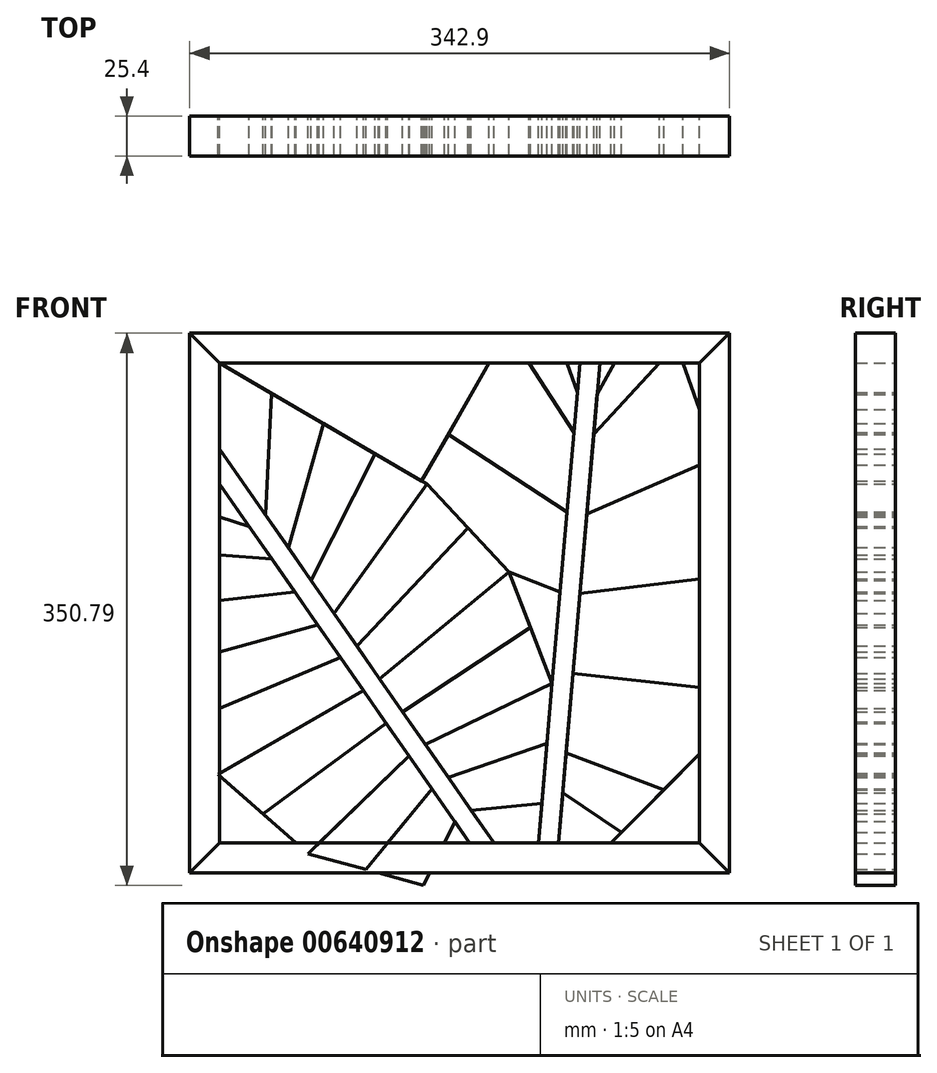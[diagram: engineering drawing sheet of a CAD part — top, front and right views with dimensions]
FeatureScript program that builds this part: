
annotation { "Feature Type Name" : "Feature", "Feature Type Description" : "" }
export const myFeature = defineFeature(function(context is Context, id is Id, definition is map)
    precondition{}
    {
        {
            var Q0;
            Q0=qCreatedBy(makeId("Front.planeOp"),FACE);
            var sketch = newSketch(context, id + "F0", { "sketchPlane" : qUnion([Q0])});
            skLineSegment(sketch, "E0.bottom", {"start": v(152.4, -152.4) * mm, "end": v(-152.4, -152.4) * mm});
            skLineSegment(sketch, "E0.top", {"start": v(152.4, 152.4) * mm, "end": v(-152.4, 152.4) * mm});
            skLineSegment(sketch, "E0.left", {"start": v(152.4, -152.4) * mm, "end": v(152.4, 152.4) * mm});
            skLineSegment(sketch, "E0.right", {"start": v(-152.4, -152.4) * mm, "end": v(-152.4, 152.4) * mm});
            skPoint(sketch, "E0.middle", {"position": v(0, 0) * mm});
            skLineSegment(sketch, "E1", {"start": v(-152.4, 152.4) * mm, "end": v(-20.79, 75.56) * mm});
            skLineSegment(sketch, "E2", {"start": v(-20.79, 75.56) * mm, "end": v(31.28, 19.93) * mm});
            skLineSegment(sketch, "E3", {"start": v(58.68, -51.18) * mm, "end": v(49.93, -152.4) * mm});
            skLineSegment(sketch, "E4.0", {"start": v(-152.4, 97.73) * mm, "end": v(21.77, -152.4) * mm});
            skLineSegment(sketch, "E5", {"start": v(31.28, 19.93) * mm, "end": v(58.68, -51.18) * mm});
            skPoint(sketch, "E6", {"position": v(-65.31, -27.33) * mm});
            skPoint(sketch, "E7", {"position": v(-79.83, -6.49) * mm});
            skPoint(sketch, "E8", {"position": v(-94.34, 14.36) * mm});
            skPoint(sketch, "E9", {"position": v(-108.86, 35.2) * mm});
            skPoint(sketch, "E10", {"position": v(-123.37, 56.05) * mm});
            skPoint(sketch, "E11", {"position": v(-50.8, -48.18) * mm});
            skPoint(sketch, "E12", {"position": v(-36.29, -69.02) * mm});
            skPoint(sketch, "E13", {"position": v(-21.77, -89.87) * mm});
            skPoint(sketch, "E14", {"position": v(-7.26, -110.71) * mm});
            skPoint(sketch, "E15", {"position": v(-137.89, 76.9) * mm});
            skPoint(sketch, "E16", {"position": v(7.26, -131.56) * mm});
            skLineSegment(sketch, "E17.0", {"start": v(-157.61, 94.1) * mm, "end": v(16.56, -156.03) * mm, "construction": true});
            skLineSegment(sketch, "E18.0", {"start": v(-162.82, 90.48) * mm, "end": v(11.35, -159.66) * mm});
            skLineSegment(sketch, "E19", {"start": v(-65.31, -27.33) * mm, "end": v(5.25, 47.75) * mm});
            skLineSegment(sketch, "E20", {"start": v(-79.83, -6.49) * mm, "end": v(-20.79, 75.56) * mm});
            skLineSegment(sketch, "E21", {"start": v(-50.8, -48.18) * mm, "end": v(31.28, 19.93) * mm});
            skLineSegment(sketch, "E22", {"start": v(-21.77, -89.87) * mm, "end": v(58.68, -51.18) * mm});
            skLineSegment(sketch, "E23", {"start": v(-86.6, 113.98) * mm, "end": v(-108.86, 35.2) * mm});
            skLineSegment(sketch, "E24", {"start": v(-94.34, 14.36) * mm, "end": v(-53.7, 94.77) * mm});
            skLineSegment(sketch, "E25", {"start": v(-123.37, 56.05) * mm, "end": v(-119.5, 133.2) * mm});
            skLineSegment(sketch, "E26", {"start": v(-137.89, 76.9) * mm, "end": v(-152.4, 152.4) * mm});
            skLineSegment(sketch, "E27", {"start": v(44.98, -15.62) * mm, "end": v(-36.29, -69.02) * mm});
            skLineSegment(sketch, "E28", {"start": v(-7.26, -110.71) * mm, "end": v(55.4, -89.14) * mm});
            skLineSegment(sketch, "E29", {"start": v(7.26, -131.56) * mm, "end": v(52.12, -127.1) * mm});
            skPoint(sketch, "E30.MirrorP", {"position": v(-32.2, -97.12) * mm});
            skPoint(sketch, "E31.MirrorP", {"position": v(-148.3, 69.63) * mm});
            skLineSegment(sketch, "E32.MirrorCS", {"start": v(-61.22, -55.43) * mm, "end": v(-153.57, -108.79) * mm});
            skLineSegment(sketch, "E33.MirrorCS", {"start": v(-148.3, 69.63) * mm, "end": v(-214.1, 109.44) * mm});
            skLineSegment(sketch, "E34.MirrorCS", {"start": v(-200.9, 34.4) * mm, "end": v(-119.28, 27.94) * mm});
            skLineSegment(sketch, "E35.MirrorCS", {"start": v(-17.68, -117.97) * mm, "end": v(-59.65, -169.25) * mm});
            skPoint(sketch, "E36.MirrorP", {"position": v(-75.74, -34.59) * mm});
            skPoint(sketch, "E37.MirrorP", {"position": v(-46.7, -76.28) * mm});
            skPoint(sketch, "E38.MirrorP", {"position": v(-90.25, -13.75) * mm});
            skLineSegment(sketch, "E39.MirrorCS", {"start": v(-153.57, -108.79) * mm, "end": v(-96.4, -159.15) * mm});
            skPoint(sketch, "E40.MirrorP", {"position": v(-104.77, 7.1) * mm});
            skLineSegment(sketch, "E41.MirrorCS", {"start": v(-96.4, -159.15) * mm, "end": v(1.58, -186.07) * mm});
            skLineSegment(sketch, "E42.MirrorCS", {"start": v(-75.74, -34.59) * mm, "end": v(-170.63, -74.72) * mm});
            skPoint(sketch, "E43.MirrorP", {"position": v(-133.8, 48.79) * mm});
            skPoint(sketch, "E44.MirrorP", {"position": v(-3.17, -138.81) * mm});
            skLineSegment(sketch, "E45.MirrorCS", {"start": v(-214.1, 109.44) * mm, "end": v(-187.69, -40.65) * mm});
            skPoint(sketch, "E46.MirrorP", {"position": v(-119.28, 27.94) * mm});
            skLineSegment(sketch, "E47.MirrorCS", {"start": v(-90.25, -13.75) * mm, "end": v(-187.69, -40.65) * mm});
            skLineSegment(sketch, "E48.MirrorCS", {"start": v(-3.17, -138.81) * mm, "end": v(-22.91, -179.34) * mm});
            skLineSegment(sketch, "E49.MirrorCS", {"start": v(-133.8, 48.79) * mm, "end": v(-207.5, 71.92) * mm});
            skLineSegment(sketch, "E50.MirrorCS", {"start": v(-104.77, 7.1) * mm, "end": v(-194.29, -3.13) * mm});
            skLineSegment(sketch, "E51.MirrorCS", {"start": v(-32.2, -97.12) * mm, "end": v(-96.4, -159.15) * mm});
            skLineSegment(sketch, "E52.MirrorCS", {"start": v(-124.98, -133.97) * mm, "end": v(-46.7, -76.28) * mm});
            skPoint(sketch, "E53.MirrorP", {"position": v(-61.22, -55.43) * mm});
            skPoint(sketch, "E54.MirrorP", {"position": v(-124.03, -86.36) * mm});
            skLineSegment(sketch, "E55.MirrorCS", {"start": v(-187.69, -40.65) * mm, "end": v(-153.57, -108.79) * mm});
            skPoint(sketch, "E56.MirrorP", {"position": v(-17.68, -117.97) * mm});
            skLineSegment(sketch, "E57", {"start": v(-46.8, 162.1) * mm, "end": v(-27.2, 88.72) * mm});
            skLineSegment(sketch, "E58.MirrorCS", {"start": v(89.49, 157.88) * mm, "end": v(63.25, -145.8) * mm});
            skPoint(sketch, "E59.MirrorP", {"position": v(69.8, -69.88) * mm});
            skLineSegment(sketch, "E60.MirrorCS", {"start": v(76.83, 158.97) * mm, "end": v(50.6, -144.7) * mm});
            skLineSegment(sketch, "E61.MirrorCS", {"start": v(89.49, 157.88) * mm, "end": v(62.68, -152.4) * mm});
            skPoint(sketch, "E62.MirrorP", {"position": v(57.16, -68.78) * mm});
            skLineSegment(sketch, "E63.MirrorCS", {"start": v(83.16, 158.42) * mm, "end": v(56.92, -145.25) * mm, "construction": true});
            skLineSegment(sketch, "E64.MirrorCS", {"start": v(87.3, 132.57) * mm, "end": v(124.47, 199.88) * mm});
            skLineSegment(sketch, "E65.MirrorCS", {"start": v(67.62, -95.18) * mm, "end": v(129.58, -118.7) * mm});
            skLineSegment(sketch, "E66.MirrorCS", {"start": v(11.7, 140.24) * mm, "end": v(70.27, 83.05) * mm});
            skPoint(sketch, "E67.MirrorP", {"position": v(72.46, 108.36) * mm});
            skPoint(sketch, "E68.MirrorP", {"position": v(82.93, 81.96) * mm});
            skLineSegment(sketch, "E69.MirrorCS", {"start": v(124.47, 199.88) * mm, "end": v(176.43, 56.61) * mm});
            skLineSegment(sketch, "E70.MirrorCS", {"start": v(65.44, -120.49) * mm, "end": v(102.76, -145.77) * mm});
            skLineSegment(sketch, "E71.MirrorCS", {"start": v(-43.58, -0.07) * mm, "end": v(-31.87, -75.36) * mm});
            skLineSegment(sketch, "E72.MirrorCS", {"start": v(-26.2, 74.12) * mm, "end": v(-43.58, -0.07) * mm});
            skPoint(sketch, "E73.MirrorP", {"position": v(80.74, 56.65) * mm});
            skLineSegment(sketch, "E74.MirrorCS", {"start": v(85.11, 107.26) * mm, "end": v(137.46, 164.07) * mm});
            skPoint(sketch, "E75.MirrorP", {"position": v(63.71, 7.13) * mm});
            skLineSegment(sketch, "E76.MirrorCS", {"start": v(57.16, -68.78) * mm, "end": v(-31.87, -75.36) * mm});
            skLineSegment(sketch, "E77.MirrorCS", {"start": v(74.65, 133.66) * mm, "end": v(49.57, 206.35) * mm});
            skLineSegment(sketch, "E78.MirrorCS", {"start": v(150.45, 128.25) * mm, "end": v(82.93, 81.96) * mm});
            skLineSegment(sketch, "E79.MirrorCS", {"start": v(76.37, 6.04) * mm, "end": v(178.63, 18.58) * mm});
            skLineSegment(sketch, "E80.MirrorCS", {"start": v(54.97, -94.09) * mm, "end": v(-10.1, -106.63) * mm});
            skPoint(sketch, "E81.MirrorP", {"position": v(65.44, -120.49) * mm});
            skPoint(sketch, "E82.MirrorP", {"position": v(52.78, -119.4) * mm});
            skLineSegment(sketch, "E83.MirrorCS", {"start": v(156.39, -91.63) * mm, "end": v(84.89, -163.81) * mm});
            skLineSegment(sketch, "E84.MirrorCS", {"start": v(32.57, 16.57) * mm, "end": v(-34.89, 37.02) * mm});
            skLineSegment(sketch, "E85.MirrorCS", {"start": v(168.61, -55.54) * mm, "end": v(72, -44.57) * mm});
            skPoint(sketch, "E86.MirrorP", {"position": v(72, -44.57) * mm});
            skLineSegment(sketch, "E87.MirrorCS", {"start": v(68.09, 57.75) * mm, "end": v(-7.25, 107.18) * mm});
            skPoint(sketch, "E88.MirrorP", {"position": v(-6.53, -1.74) * mm});
            skPoint(sketch, "E89.MirrorP", {"position": v(74.65, 133.66) * mm});
            skLineSegment(sketch, "E90.MirrorCS", {"start": v(49.57, 206.35) * mm, "end": v(-26.2, 74.12) * mm});
            skLineSegment(sketch, "E91.MirrorCS", {"start": v(176.43, 56.61) * mm, "end": v(180.84, -19.46) * mm});
            skLineSegment(sketch, "E92.MirrorCS", {"start": v(72.46, 108.36) * mm, "end": v(30.63, 173.3) * mm});
            skPoint(sketch, "E93.MirrorP", {"position": v(54.97, -94.09) * mm});
            skPoint(sketch, "E94.MirrorP", {"position": v(70.27, 83.05) * mm});
            skLineSegment(sketch, "E95.MirrorCS", {"start": v(78.55, 31.35) * mm, "end": v(176.43, 56.61) * mm});
            skPoint(sketch, "E96.MirrorP", {"position": v(65.9, 32.44) * mm});
            skLineSegment(sketch, "E97.MirrorCS", {"start": v(52.78, -119.4) * mm, "end": v(11.67, -137.9) * mm});
            skLineSegment(sketch, "E98.MirrorCS", {"start": v(-37.73, -37.72) * mm, "end": v(59.34, -43.48) * mm});
            skPoint(sketch, "E99.MirrorP", {"position": v(85.11, 107.26) * mm});
            skPoint(sketch, "E100.MirrorP", {"position": v(78.55, 31.35) * mm});
            skPoint(sketch, "E101.MirrorP", {"position": v(76.37, 6.04) * mm});
            skLineSegment(sketch, "E102.MirrorCS", {"start": v(-14.47, 68.82) * mm, "end": v(-26.2, 74.12) * mm});
            skPoint(sketch, "E103.MirrorP", {"position": v(59.34, -43.48) * mm});
            skPoint(sketch, "E104.MirrorP", {"position": v(74.18, -19.26) * mm});
            skLineSegment(sketch, "E105.MirrorCS", {"start": v(69.8, -69.88) * mm, "end": v(156.39, -91.63) * mm});
            skPoint(sketch, "E106.MirrorP", {"position": v(61.53, -18.17) * mm});
            skLineSegment(sketch, "E107.MirrorCS", {"start": v(80.74, 56.65) * mm, "end": v(163.44, 92.43) * mm});
            skLineSegment(sketch, "E108.MirrorCS", {"start": v(61.53, -18.17) * mm, "end": v(-43.58, -0.07) * mm});
            skLineSegment(sketch, "E109.MirrorCS", {"start": v(-31.87, -75.36) * mm, "end": v(26.19, -158.74) * mm});
            skLineSegment(sketch, "E110.MirrorCS", {"start": v(74.18, -19.26) * mm, "end": v(180.84, -19.46) * mm});
            skPoint(sketch, "E111.MirrorP", {"position": v(87.3, 132.57) * mm});
            skPoint(sketch, "E112.MirrorP", {"position": v(67.62, -95.18) * mm});
            skLineSegment(sketch, "E113.MirrorCS", {"start": v(180.84, -19.46) * mm, "end": v(156.39, -91.63) * mm});
            skPoint(sketch, "E114.MirrorP", {"position": v(144.05, -14.75) * mm});
            skPoint(sketch, "E115.MirrorP", {"position": v(68.09, 57.75) * mm});
            skPoint(sketch, "E116.orphan", {"position": v(63.25, -145.8) * mm});
            skLineSegment(sketch, "E117", {"start": v(31.28, 19.93) * mm, "end": v(63.71, 7.13) * mm});
            skLineSegment(sketch, "E118", {"start": v(-20.79, 75.56) * mm, "end": v(65.9, 32.44) * mm});
            skLineSegment(sketch, "E119.bottom", {"start": v(171.45, -171.45) * mm, "end": v(-171.45, -171.45) * mm});
            skLineSegment(sketch, "E119.top", {"start": v(171.45, 171.45) * mm, "end": v(-171.45, 171.45) * mm});
            skLineSegment(sketch, "E119.left", {"start": v(171.45, -171.45) * mm, "end": v(171.45, 171.45) * mm});
            skLineSegment(sketch, "E119.right", {"start": v(-171.45, -171.45) * mm, "end": v(-171.45, 171.45) * mm});
            skLineSegment(sketch, "E120", {"start": v(-152.4, 152.4) * mm, "end": v(-171.45, 171.45) * mm});
            skLineSegment(sketch, "E121", {"start": v(152.4, 152.4) * mm, "end": v(171.45, 171.45) * mm});
            skLineSegment(sketch, "E122", {"start": v(152.4, -152.4) * mm, "end": v(171.45, -171.45) * mm});
            skLineSegment(sketch, "E123", {"start": v(-152.4, -152.4) * mm, "end": v(-171.45, -171.45) * mm});
            skSolve(sketch);
        }
        {
            var Q0;
            {var subQ0=sQuery(id+"F0.wireOp",EDGE,"E33.MirrorCS");var subQ1=sQuery(id+"F0.wireOp",EDGE,"E0.right");var subQ2=makeQuery(id+"F0.imprint","INTERSECT",VERTEX,{"derivedFrom":[subQ1,subQ0]});Q0=makeQuery(id+"F0.imprint","IMPRINT",FACE,{"disambiguationData":[TD([[makeQuery(id+"F0.imprint","IMPRINT",EDGE,{"disambiguationData":[TD([[subQ2,1.0]])],"derivedFrom":subQ1}),-1.0]])]});}
            var Q1;
            {var subQ0=sQuery(id+"F0.wireOp",EDGE,"E18.0");var subQ1=sQuery(id+"F0.wireOp",EDGE,"E0.right");var subQ2=makeQuery(id+"F0.imprint","INTERSECT",VERTEX,{"derivedFrom":[subQ1,subQ0]});Q1=makeQuery(id+"F0.imprint","IMPRINT",FACE,{"disambiguationData":[TD([[makeQuery(id+"F0.imprint","IMPRINT",EDGE,{"disambiguationData":[TD([[subQ2,1.0]])],"derivedFrom":subQ1}),-1.0]])]});}
            extrude(context, id + "F1", {"entities" : qUnion([Q0, Q1]), "depth" : 25.4 * mm, "offsetDistance" : 25.4 * mm});
        }
        {
            var Q0;
            {var subQ0=sQuery(id+"F0.wireOp",EDGE,"E26");Q0=makeQuery(id+"F0.imprint","IMPRINT",FACE,{"disambiguationData":[TD([[makeQuery(id+"F0.imprint","IMPRINT",EDGE,{"derivedFrom":subQ0}),1.0]])]});}
            var Q1;
            {var subQ2=sQuery(id+"F0.wireOp",EDGE,"E25");Q1=makeQuery(id+"F0.imprint","IMPRINT",FACE,{"disambiguationData":[TD([[makeQuery(id+"F0.imprint","IMPRINT",EDGE,{"derivedFrom":subQ2}),1.0]])]});}
            extrude(context, id + "F2", {"entities" : qUnion([Q0, Q1]), "depth" : 25.4 * mm, "offsetDistance" : 25.4 * mm});
        }
        {
            var Q0;
            {var subQ3=sQuery(id+"F0.wireOp",EDGE,"E4.0");var subQ9=sQuery(id+"F0.wireOp",EDGE,"E0.right");var subQ16=makeQuery(id+"F0.imprint","INTERSECT",VERTEX,{"derivedFrom":[subQ9,subQ3]});Q0=makeQuery(id+"F0.imprint","IMPRINT",FACE,{"disambiguationData":[TD([[makeQuery(id+"F0.imprint","IMPRINT",EDGE,{"disambiguationData":[TD([[subQ16,1.0]])],"derivedFrom":subQ9}),-1.0]])]});}
            var Q1;
            {var subQ4=sQuery(id+"F0.wireOp",EDGE,"E4.0");var subQ10=makeQuery(id+"F0.imprint","INTERSECT",VERTEX,{"derivedFrom":[subQ4,sQuery(id+"F0.wireOp",EDGE,"E21")]});Q1=makeQuery(id+"F0.imprint","IMPRINT",FACE,{"disambiguationData":[TD([[makeQuery(id+"F0.imprint","IMPRINT",EDGE,{"disambiguationData":[TD([[subQ10,1.0]])],"derivedFrom":subQ4}),-1.0]])]});}
            var Q2;
            {var subQ9=sQuery(id+"F0.wireOp",EDGE,"E4.0");var subQ10=makeQuery(id+"F0.imprint","INTERSECT",VERTEX,{"derivedFrom":[subQ9,sQuery(id+"F0.wireOp",EDGE,"E22")]});Q2=makeQuery(id+"F0.imprint","IMPRINT",FACE,{"disambiguationData":[TD([[makeQuery(id+"F0.imprint","IMPRINT",EDGE,{"disambiguationData":[TD([[subQ10,1.0]])],"derivedFrom":subQ9}),-1.0]])]});}
            var Q3;
            {var subQ0=sQuery(id+"F0.wireOp",EDGE,"E4.0");var subQ1=makeQuery(id+"F0.imprint","INTERSECT",VERTEX,{"derivedFrom":[subQ0,sQuery(id+"F0.wireOp",EDGE,"E19")]});Q3=makeQuery(id+"F0.imprint","IMPRINT",FACE,{"disambiguationData":[TD([[makeQuery(id+"F0.imprint","IMPRINT",EDGE,{"disambiguationData":[TD([[subQ1,1.0]])],"derivedFrom":subQ0}),-1.0]])]});}
            var Q4;
            {var subQ2=sQuery(id+"F0.wireOp",EDGE,"E4.0");var subQ4=makeQuery(id+"F0.imprint","INTERSECT",VERTEX,{"derivedFrom":[subQ2,sQuery(id+"F0.wireOp",EDGE,"E28")]});Q4=makeQuery(id+"F0.imprint","IMPRINT",FACE,{"disambiguationData":[TD([[makeQuery(id+"F0.imprint","IMPRINT",EDGE,{"disambiguationData":[TD([[subQ4,1.0]])],"derivedFrom":subQ2}),-1.0]])]});}
            var Q5;
            {var subQ0=sQuery(id+"F0.wireOp",EDGE,"E18.0");var subQ1=makeQuery(id+"F0.imprint","INTERSECT",VERTEX,{"derivedFrom":[sQuery(id+"F0.wireOp",EDGE,"E35.MirrorCS"),subQ0]});Q5=makeQuery(id+"F0.imprint","IMPRINT",FACE,{"disambiguationData":[TD([[makeQuery(id+"F0.imprint","IMPRINT",EDGE,{"disambiguationData":[TD([[subQ1,1.0]])],"derivedFrom":subQ0}),1.0]])]});}
            var Q6;
            {var subQ0=sQuery(id+"F0.wireOp",EDGE,"E4.0");var subQ1=sQuery(id+"F0.wireOp",EDGE,"E0.bottom");var subQ2=makeQuery(id+"F0.imprint","INTERSECT",VERTEX,{"derivedFrom":[subQ1,subQ0]});Q6=makeQuery(id+"F0.imprint","IMPRINT",FACE,{"disambiguationData":[TD([[makeQuery(id+"F0.imprint","IMPRINT",EDGE,{"disambiguationData":[TD([[subQ2,-1.0]])],"derivedFrom":subQ1}),-1.0]])]});}
            extrude(context, id + "F3", {"entities" : qUnion([Q0, Q1, Q2, Q3, Q4, Q5, Q6]), "depth" : 25.4 * mm, "offsetDistance" : 25.4 * mm});
        }
        {
            var Q0;
            {var subQ0=sQuery(id+"F0.wireOp",EDGE,"E34.MirrorCS");var subQ1=sQuery(id+"F0.wireOp",EDGE,"E0.right");var subQ2=makeQuery(id+"F0.imprint","INTERSECT",VERTEX,{"derivedFrom":[subQ1,subQ0]});Q0=makeQuery(id+"F0.imprint","IMPRINT",FACE,{"disambiguationData":[TD([[makeQuery(id+"F0.imprint","IMPRINT",EDGE,{"disambiguationData":[TD([[subQ2,-1.0]])],"derivedFrom":subQ1}),-1.0]])]});}
            extrude(context, id + "F4", {"entities" : qUnion([Q0]), "depth" : 25.4 * mm, "offsetDistance" : 25.4 * mm});
        }
        {
            var Q0;
            {var subQ0=sQuery(id+"F0.wireOp",EDGE,"E50.MirrorCS");var subQ1=sQuery(id+"F0.wireOp",EDGE,"E0.right");var subQ2=makeQuery(id+"F0.imprint","INTERSECT",VERTEX,{"derivedFrom":[subQ1,subQ0]});Q0=makeQuery(id+"F0.imprint","IMPRINT",FACE,{"disambiguationData":[TD([[makeQuery(id+"F0.imprint","IMPRINT",EDGE,{"disambiguationData":[TD([[subQ2,-1.0]])],"derivedFrom":subQ1}),-1.0]])]});}
            extrude(context, id + "F5", {"entities" : qUnion([Q0]), "depth" : 25.4 * mm, "offsetDistance" : 25.4 * mm});
        }
        {
            var Q0;
            {var subQ0=sQuery(id+"F0.wireOp",EDGE,"E47.MirrorCS");var subQ1=sQuery(id+"F0.wireOp",EDGE,"E0.right");var subQ2=makeQuery(id+"F0.imprint","INTERSECT",VERTEX,{"derivedFrom":[subQ1,subQ0]});Q0=makeQuery(id+"F0.imprint","IMPRINT",FACE,{"disambiguationData":[TD([[makeQuery(id+"F0.imprint","IMPRINT",EDGE,{"disambiguationData":[TD([[subQ2,-1.0]])],"derivedFrom":subQ1}),-1.0]])]});}
            extrude(context, id + "F6", {"entities" : qUnion([Q0]), "depth" : 25.4 * mm, "offsetDistance" : 25.4 * mm});
        }
        {
            var Q0;
            {var subQ5=sQuery(id+"F0.wireOp",EDGE,"E42.MirrorCS");var subQ7=sQuery(id+"F0.wireOp",EDGE,"E0.right");var subQ9=makeQuery(id+"F0.imprint","INTERSECT",VERTEX,{"derivedFrom":[subQ7,subQ5]});Q0=makeQuery(id+"F0.imprint","IMPRINT",FACE,{"disambiguationData":[TD([[makeQuery(id+"F0.imprint","IMPRINT",EDGE,{"disambiguationData":[TD([[subQ9,-1.0]])],"derivedFrom":subQ7}),-1.0]])]});}
            var Q1;
            {var subQ0=sQuery(id+"F0.wireOp",EDGE,"E18.0");var subQ1=sQuery(id+"F0.wireOp",EDGE,"E42.MirrorCS");var subQ2=makeQuery(id+"F0.imprint","INTERSECT",VERTEX,{"derivedFrom":[subQ1,subQ0]});Q1=makeQuery(id+"F0.imprint","IMPRINT",FACE,{"disambiguationData":[TD([[makeQuery(id+"F0.imprint","IMPRINT",EDGE,{"disambiguationData":[TD([[subQ2,-1.0]])],"derivedFrom":subQ1}),-1.0]])]});}
            extrude(context, id + "F7", {"entities" : qUnion([Q0, Q1]), "depth" : 25.4 * mm, "offsetDistance" : 25.4 * mm});
        }
        {
            var Q0;
            {var subQ0=sQuery(id+"F0.wireOp",EDGE,"E32.MirrorCS");var subQ1=sQuery(id+"F0.wireOp",EDGE,"E0.right");var subQ2=makeQuery(id+"F0.imprint","INTERSECT",VERTEX,{"derivedFrom":[subQ1,subQ0]});Q0=makeQuery(id+"F0.imprint","IMPRINT",FACE,{"disambiguationData":[TD([[makeQuery(id+"F0.imprint","IMPRINT",EDGE,{"disambiguationData":[TD([[subQ2,-1.0]])],"derivedFrom":subQ1}),-1.0]])]});}
            extrude(context, id + "F8", {"entities" : qUnion([Q0]), "depth" : 25.4 * mm, "offsetDistance" : 25.4 * mm});
        }
        {
            var Q0;
            {var subQ1=sQuery(id+"F0.wireOp",EDGE,"E39.MirrorCS");var subQ5=sQuery(id+"F0.wireOp",EDGE,"E0.right");var subQ6=makeQuery(id+"F0.imprint","INTERSECT",VERTEX,{"derivedFrom":[subQ5,subQ1]});Q0=makeQuery(id+"F0.imprint","IMPRINT",FACE,{"disambiguationData":[TD([[makeQuery(id+"F0.imprint","IMPRINT",EDGE,{"disambiguationData":[TD([[subQ6,-1.0]])],"derivedFrom":subQ5}),-1.0]])]});}
            var Q1;
            {var subQ0=sQuery(id+"F0.wireOp",EDGE,"E18.0");var subQ1=sQuery(id+"F0.wireOp",EDGE,"E32.MirrorCS");var subQ2=makeQuery(id+"F0.imprint","INTERSECT",VERTEX,{"derivedFrom":[subQ1,subQ0]});Q1=makeQuery(id+"F0.imprint","IMPRINT",FACE,{"disambiguationData":[TD([[makeQuery(id+"F0.imprint","IMPRINT",EDGE,{"disambiguationData":[TD([[subQ2,-1.0]])],"derivedFrom":subQ1}),1.0]])]});}
            extrude(context, id + "F9", {"entities" : qUnion([Q0, Q1]), "depth" : 25.4 * mm, "offsetDistance" : 25.4 * mm});
        }
        {
            var Q0;
            {var subQ5=sQuery(id+"F0.wireOp",EDGE,"E52.MirrorCS");Q0=makeQuery(id+"F0.imprint","IMPRINT",FACE,{"disambiguationData":[TD([[makeQuery(id+"F0.imprint","IMPRINT",EDGE,{"derivedFrom":subQ5}),-1.0]])]});}
            extrude(context, id + "F10", {"entities" : qUnion([Q0]), "depth" : 25.4 * mm, "offsetDistance" : 25.4 * mm});
        }
        {
            var Q0;
            {var subQ0=sQuery(id+"F0.wireOp",EDGE,"E18.0");var subQ1=sQuery(id+"F0.wireOp",EDGE,"E51.MirrorCS");var subQ2=makeQuery(id+"F0.imprint","INTERSECT",VERTEX,{"derivedFrom":[subQ1,subQ0]});Q0=makeQuery(id+"F0.imprint","IMPRINT",FACE,{"disambiguationData":[TD([[makeQuery(id+"F0.imprint","IMPRINT",EDGE,{"disambiguationData":[TD([[subQ2,-1.0]])],"derivedFrom":subQ1}),1.0]])]});}
            var Q1;
            {var subQ3=sQuery(id+"F0.wireOp",EDGE,"E35.MirrorCS");var subQ8=sQuery(id+"F0.wireOp",EDGE,"E18.0");var subQ10=makeQuery(id+"F0.imprint","INTERSECT",VERTEX,{"derivedFrom":[subQ3,subQ8]});Q1=makeQuery(id+"F0.imprint","IMPRINT",FACE,{"disambiguationData":[TD([[makeQuery(id+"F0.imprint","IMPRINT",EDGE,{"disambiguationData":[TD([[subQ10,-1.0]])],"derivedFrom":subQ3}),-1.0]])]});}
            var Q2;
            {var subQ0=sQuery(id+"F0.wireOp",EDGE,"cba4c753-2e67-4180-9106-f9a73cf6535f38.MirrorCS");var subQ1=sQuery(id+"F0.wireOp",EDGE,"E0.bottom");var subQ2=makeQuery(id+"F0.imprint","INTERSECT",VERTEX,{"derivedFrom":[subQ1,subQ0]});Q2=makeQuery(id+"F0.imprint","IMPRINT",FACE,{"disambiguationData":[TD([[makeQuery(id+"F0.imprint","IMPRINT",EDGE,{"disambiguationData":[TD([[subQ2,1.0]])],"derivedFrom":subQ1}),-1.0]])]});}
            var Q3;
            {var subQ0=sQuery(id+"F0.wireOp",EDGE,"cba4c753-2e67-4180-9106-f9a73cf6535f38.MirrorCS");var subQ1=sQuery(id+"F0.wireOp",EDGE,"E0.bottom");var subQ2=makeQuery(id+"F0.imprint","INTERSECT",VERTEX,{"derivedFrom":[subQ1,subQ0]});Q3=makeQuery(id+"F0.imprint","IMPRINT",FACE,{"disambiguationData":[TD([[makeQuery(id+"F0.imprint","IMPRINT",EDGE,{"disambiguationData":[TD([[subQ2,-1.0]])],"derivedFrom":subQ1}),-1.0]])]});}
            extrude(context, id + "F11", {"entities" : qUnion([Q0, Q1, Q2, Q3]), "depth" : 25.4 * mm, "offsetDistance" : 25.4 * mm});
        }
        {
            var Q0;
            {var subQ0=sQuery(id+"F0.wireOp",EDGE,"cba4c753-2e67-4180-9106-f9a73cf6535f1.MirrorCS");var subQ1=sQuery(id+"F0.wireOp",EDGE,"E0.bottom");var subQ2=makeQuery(id+"F0.imprint","INTERSECT",VERTEX,{"derivedFrom":[subQ1,subQ0]});Q0=makeQuery(id+"F0.imprint","IMPRINT",FACE,{"disambiguationData":[TD([[makeQuery(id+"F0.imprint","IMPRINT",EDGE,{"disambiguationData":[TD([[subQ2,-1.0]])],"derivedFrom":subQ1}),-1.0]])]});}
            var Q1;
            {var subQ0=sQuery(id+"F0.wireOp",EDGE,"E18.0");var subQ1=sQuery(id+"F0.wireOp",EDGE,"E35.MirrorCS");var subQ2=makeQuery(id+"F0.imprint","INTERSECT",VERTEX,{"derivedFrom":[subQ1,subQ0]});Q1=makeQuery(id+"F0.imprint","IMPRINT",FACE,{"disambiguationData":[TD([[makeQuery(id+"F0.imprint","IMPRINT",EDGE,{"disambiguationData":[TD([[subQ2,-1.0]])],"derivedFrom":subQ1}),1.0]])]});}
            var Q2;
            {var subQ2=sQuery(id+"F0.wireOp",EDGE,"E0.bottom");var subQ6=sQuery(id+"F0.wireOp",EDGE,"cba4c753-2e67-4180-9106-f9a73cf6535f3.MirrorCS");var subQ8=makeQuery(id+"F0.imprint","INTERSECT",VERTEX,{"derivedFrom":[subQ2,subQ6]});Q2=makeQuery(id+"F0.imprint","IMPRINT",FACE,{"disambiguationData":[TD([[makeQuery(id+"F0.imprint","IMPRINT",EDGE,{"disambiguationData":[TD([[subQ8,-1.0]])],"derivedFrom":subQ2}),-1.0]])]});}
            var Q3;
            {var subQ0=sQuery(id+"F0.wireOp",EDGE,"E18.0");var subQ1=sQuery(id+"F0.wireOp",EDGE,"E48.MirrorCS");var subQ2=makeQuery(id+"F0.imprint","INTERSECT",VERTEX,{"derivedFrom":[subQ1,subQ0]});Q3=makeQuery(id+"F0.imprint","IMPRINT",FACE,{"disambiguationData":[TD([[makeQuery(id+"F0.imprint","IMPRINT",EDGE,{"disambiguationData":[TD([[subQ2,-1.0]])],"derivedFrom":subQ1}),-1.0]])]});}
            var Q4;
            {var subQ0=sQuery(id+"F0.wireOp",EDGE,"cba4c753-2e67-4180-9106-f9a73cf6535f3.MirrorCS");var subQ1=sQuery(id+"F0.wireOp",EDGE,"E0.bottom");var subQ2=makeQuery(id+"F0.imprint","INTERSECT",VERTEX,{"derivedFrom":[subQ1,subQ0]});Q4=makeQuery(id+"F0.imprint","IMPRINT",FACE,{"disambiguationData":[TD([[makeQuery(id+"F0.imprint","IMPRINT",EDGE,{"disambiguationData":[TD([[subQ2,1.0]])],"derivedFrom":subQ1}),-1.0]])]});}
            var Q5;
            {var subQ0=sQuery(id+"F0.wireOp",EDGE,"cba4c753-2e67-4180-9106-f9a73cf6535f26.MirrorCS");var subQ1=sQuery(id+"F0.wireOp",EDGE,"E0.bottom");var subQ2=makeQuery(id+"F0.imprint","INTERSECT",VERTEX,{"derivedFrom":[subQ1,subQ0]});Q5=makeQuery(id+"F0.imprint","IMPRINT",FACE,{"disambiguationData":[TD([[makeQuery(id+"F0.imprint","IMPRINT",EDGE,{"disambiguationData":[TD([[subQ2,-1.0]])],"derivedFrom":subQ1}),-1.0]])]});}
            var Q6;
            {var subQ0=sQuery(id+"F0.wireOp",EDGE,"E18.0");var subQ1=sQuery(id+"F0.wireOp",EDGE,"E0.bottom");var subQ2=makeQuery(id+"F0.imprint","INTERSECT",VERTEX,{"derivedFrom":[subQ1,subQ0]});Q6=makeQuery(id+"F0.imprint","IMPRINT",FACE,{"disambiguationData":[TD([[makeQuery(id+"F0.imprint","IMPRINT",EDGE,{"disambiguationData":[TD([[subQ2,-1.0]])],"derivedFrom":subQ1}),-1.0]])]});}
            extrude(context, id + "F12", {"entities" : qUnion([Q0, Q1, Q2, Q3, Q4, Q5, Q6]), "depth" : 25.4 * mm, "offsetDistance" : 25.4 * mm});
        }
        {
            var Q0;
            {var subQ0=sQuery(id+"F0.wireOp",EDGE,"E23");Q0=makeQuery(id+"F0.imprint","IMPRINT",FACE,{"disambiguationData":[TD([[makeQuery(id+"F0.imprint","IMPRINT",EDGE,{"derivedFrom":subQ0}),-1.0]])]});}
            extrude(context, id + "F13", {"entities" : qUnion([Q0]), "depth" : 25.4 * mm, "offsetDistance" : 25.4 * mm});
        }
        {
            var Q0;
            {var subQ0=sQuery(id+"F0.wireOp",EDGE,"E23");Q0=makeQuery(id+"F0.imprint","IMPRINT",FACE,{"disambiguationData":[TD([[makeQuery(id+"F0.imprint","IMPRINT",EDGE,{"derivedFrom":subQ0}),1.0]])]});}
            extrude(context, id + "F14", {"entities" : qUnion([Q0]), "depth" : 25.4 * mm, "offsetDistance" : 25.4 * mm});
        }
        {
            var Q0;
            {var subQ0=sQuery(id+"F0.wireOp",EDGE,"E24");Q0=makeQuery(id+"F0.imprint","IMPRINT",FACE,{"disambiguationData":[TD([[makeQuery(id+"F0.imprint","IMPRINT",EDGE,{"derivedFrom":subQ0}),-1.0]])]});}
            var Q1;
            {var subQ0=sQuery(id+"F0.wireOp",EDGE,"E72.MirrorCS");var subQ1=sQuery(id+"F0.wireOp",EDGE,"E20");var subQ2=makeQuery(id+"F0.imprint","INTERSECT",VERTEX,{"derivedFrom":[subQ1,subQ0]});Q1=makeQuery(id+"F0.imprint","IMPRINT",FACE,{"disambiguationData":[TD([[makeQuery(id+"F0.imprint","IMPRINT",EDGE,{"disambiguationData":[TD([[subQ2,-1.0]])],"derivedFrom":subQ1}),1.0]])]});}
            var Q2;
            {var subQ1=sQuery(id+"F0.wireOp",EDGE,"E1");var subQ3=sQuery(id+"F0.wireOp",EDGE,"E90.MirrorCS");var subQ4=makeQuery(id+"F0.imprint","INTERSECT",VERTEX,{"derivedFrom":[subQ1,subQ3]});Q2=makeQuery(id+"F0.imprint","IMPRINT",FACE,{"disambiguationData":[TD([[makeQuery(id+"F0.imprint","IMPRINT",EDGE,{"disambiguationData":[TD([[subQ4,-1.0]])],"derivedFrom":subQ1}),-1.0]])]});}
            extrude(context, id + "F15", {"entities" : qUnion([Q0, Q1, Q2]), "depth" : 25.4 * mm, "offsetDistance" : 25.4 * mm});
        }
        {
            var Q0;
            {var subQ0=sQuery(id+"F0.wireOp",EDGE,"E20");var subQ1=sQuery(id+"F0.wireOp",EDGE,"E4.0");var subQ2=makeQuery(id+"F0.imprint","INTERSECT",VERTEX,{"derivedFrom":[subQ1,subQ0]});Q0=makeQuery(id+"F0.imprint","IMPRINT",FACE,{"disambiguationData":[TD([[makeQuery(id+"F0.imprint","IMPRINT",EDGE,{"disambiguationData":[TD([[subQ2,-1.0]])],"derivedFrom":subQ1}),1.0]])]});}
            var Q1;
            {var subQ1=sQuery(id+"F0.wireOp",EDGE,"E4.0");var subQ7=sQuery(id+"F0.wireOp",EDGE,"E19");var subQ8=makeQuery(id+"F0.imprint","INTERSECT",VERTEX,{"derivedFrom":[subQ1,subQ7]});Q1=makeQuery(id+"F0.imprint","IMPRINT",FACE,{"disambiguationData":[TD([[makeQuery(id+"F0.imprint","IMPRINT",EDGE,{"disambiguationData":[TD([[subQ8,1.0]])],"derivedFrom":subQ1}),1.0]])]});}
            var Q2;
            {var subQ0=sQuery(id+"F0.wireOp",EDGE,"cba4c753-2e67-4180-9106-f9a73cf6535f45.MirrorCS");var subQ1=sQuery(id+"F0.wireOp",EDGE,"E19");var subQ2=makeQuery(id+"F0.imprint","INTERSECT",VERTEX,{"derivedFrom":[subQ1,subQ0]});Q2=makeQuery(id+"F0.imprint","IMPRINT",FACE,{"disambiguationData":[TD([[makeQuery(id+"F0.imprint","IMPRINT",EDGE,{"disambiguationData":[TD([[subQ2,-1.0]])],"derivedFrom":subQ1}),1.0]])]});}
            var Q3;
            {var subQ0=sQuery(id+"F0.wireOp",EDGE,"cba4c753-2e67-4180-9106-f9a73cf6535f41.MirrorCS");var subQ1=sQuery(id+"F0.wireOp",EDGE,"E19");var subQ2=makeQuery(id+"F0.imprint","INTERSECT",VERTEX,{"derivedFrom":[subQ1,subQ0]});Q3=makeQuery(id+"F0.imprint","IMPRINT",FACE,{"disambiguationData":[TD([[makeQuery(id+"F0.imprint","IMPRINT",EDGE,{"disambiguationData":[TD([[subQ2,-1.0]])],"derivedFrom":subQ1}),1.0]])]});}
            var Q4;
            {var subQ0=sQuery(id+"F0.wireOp",EDGE,"E108.MirrorCS");var subQ1=sQuery(id+"F0.wireOp",EDGE,"E19");var subQ2=makeQuery(id+"F0.imprint","INTERSECT",VERTEX,{"derivedFrom":[subQ1,subQ0]});Q4=makeQuery(id+"F0.imprint","IMPRINT",FACE,{"disambiguationData":[TD([[makeQuery(id+"F0.imprint","IMPRINT",EDGE,{"disambiguationData":[TD([[subQ2,-1.0]])],"derivedFrom":subQ1}),1.0]])]});}
            var Q5;
            {var subQ7=sQuery(id+"F0.wireOp",EDGE,"E19");var subQ8=sQuery(id+"F0.wireOp",EDGE,"E2");var subQ9=makeQuery(id+"F0.imprint","INTERSECT",VERTEX,{"derivedFrom":[subQ8,subQ7]});Q5=makeQuery(id+"F0.imprint","IMPRINT",FACE,{"disambiguationData":[TD([[makeQuery(id+"F0.imprint","IMPRINT",EDGE,{"disambiguationData":[TD([[subQ9,1.0]])],"derivedFrom":subQ8}),-1.0]])]});}
            var Q6;
            {var subQ1=sQuery(id+"F0.wireOp",EDGE,"E2");var subQ3=sQuery(id+"F0.wireOp",EDGE,"E102.MirrorCS");var subQ4=makeQuery(id+"F0.imprint","INTERSECT",VERTEX,{"derivedFrom":[subQ1,subQ3]});Q6=makeQuery(id+"F0.imprint","IMPRINT",FACE,{"disambiguationData":[TD([[makeQuery(id+"F0.imprint","IMPRINT",EDGE,{"disambiguationData":[TD([[subQ4,-1.0]])],"derivedFrom":subQ3}),-1.0]])]});}
            extrude(context, id + "F16", {"entities" : qUnion([Q0, Q1, Q2, Q3, Q4, Q5, Q6]), "depth" : 25.4 * mm, "offsetDistance" : 25.4 * mm});
        }
        {
            var Q0;
            {var subQ0=sQuery(id+"F0.wireOp",EDGE,"cba4c753-2e67-4180-9106-f9a73cf6535f41.MirrorCS");var subQ1=sQuery(id+"F0.wireOp",EDGE,"E19");var subQ2=makeQuery(id+"F0.imprint","INTERSECT",VERTEX,{"derivedFrom":[subQ1,subQ0]});Q0=makeQuery(id+"F0.imprint","IMPRINT",FACE,{"disambiguationData":[TD([[makeQuery(id+"F0.imprint","IMPRINT",EDGE,{"disambiguationData":[TD([[subQ2,-1.0]])],"derivedFrom":subQ1}),-1.0]])]});}
            var Q1;
            {var subQ0=sQuery(id+"F0.wireOp",EDGE,"cba4c753-2e67-4180-9106-f9a73cf6535f45.MirrorCS");var subQ1=sQuery(id+"F0.wireOp",EDGE,"E19");var subQ2=makeQuery(id+"F0.imprint","INTERSECT",VERTEX,{"derivedFrom":[subQ1,subQ0]});Q1=makeQuery(id+"F0.imprint","IMPRINT",FACE,{"disambiguationData":[TD([[makeQuery(id+"F0.imprint","IMPRINT",EDGE,{"disambiguationData":[TD([[subQ2,-1.0]])],"derivedFrom":subQ1}),-1.0]])]});}
            var Q2;
            {var subQ1=sQuery(id+"F0.wireOp",EDGE,"E4.0");var subQ5=sQuery(id+"F0.wireOp",EDGE,"E19");var subQ6=makeQuery(id+"F0.imprint","INTERSECT",VERTEX,{"derivedFrom":[subQ1,subQ5]});Q2=makeQuery(id+"F0.imprint","IMPRINT",FACE,{"disambiguationData":[TD([[makeQuery(id+"F0.imprint","IMPRINT",EDGE,{"disambiguationData":[TD([[subQ6,-1.0]])],"derivedFrom":subQ1}),1.0]])]});}
            var Q3;
            {var subQ0=sQuery(id+"F0.wireOp",EDGE,"E21");var subQ1=sQuery(id+"F0.wireOp",EDGE,"E4.0");var subQ2=makeQuery(id+"F0.imprint","INTERSECT",VERTEX,{"derivedFrom":[subQ1,subQ0]});Q3=makeQuery(id+"F0.imprint","IMPRINT",FACE,{"disambiguationData":[TD([[makeQuery(id+"F0.imprint","IMPRINT",EDGE,{"disambiguationData":[TD([[subQ2,1.0]])],"derivedFrom":subQ1}),1.0]])]});}
            extrude(context, id + "F17", {"entities" : qUnion([Q0, Q1, Q2, Q3]), "depth" : 25.4 * mm, "offsetDistance" : 25.4 * mm});
        }
        {
            var Q0;
            {var subQ1=sQuery(id+"F0.wireOp",EDGE,"E5");var subQ3=sQuery(id+"F0.wireOp",EDGE,"E60.MirrorCS");var subQ4=makeQuery(id+"F0.imprint","INTERSECT",VERTEX,{"derivedFrom":[subQ1,subQ3]});Q0=makeQuery(id+"F0.imprint","IMPRINT",FACE,{"disambiguationData":[TD([[makeQuery(id+"F0.imprint","IMPRINT",EDGE,{"disambiguationData":[TD([[subQ4,-1.0]])],"derivedFrom":subQ3}),1.0]])]});}
            var Q1;
            {var subQ1=sQuery(id+"F0.wireOp",EDGE,"E5");var subQ3=sQuery(id+"F0.wireOp",EDGE,"E84.MirrorCS");var subQ4=makeQuery(id+"F0.imprint","INTERSECT",VERTEX,{"derivedFrom":[subQ1,subQ3]});Q1=makeQuery(id+"F0.imprint","IMPRINT",FACE,{"disambiguationData":[TD([[makeQuery(id+"F0.imprint","IMPRINT",EDGE,{"disambiguationData":[TD([[subQ4,-1.0]])],"derivedFrom":subQ3}),-1.0]])]});}
            var Q2;
            {var subQ2=sQuery(id+"F0.wireOp",EDGE,"E21");var subQ4=sQuery(id+"F0.wireOp",EDGE,"E4.0");var subQ5=makeQuery(id+"F0.imprint","INTERSECT",VERTEX,{"derivedFrom":[subQ4,subQ2]});Q2=makeQuery(id+"F0.imprint","IMPRINT",FACE,{"disambiguationData":[TD([[makeQuery(id+"F0.imprint","IMPRINT",EDGE,{"disambiguationData":[TD([[subQ5,-1.0]])],"derivedFrom":subQ4}),1.0]])]});}
            var Q3;
            {var subQ5=sQuery(id+"F0.wireOp",EDGE,"E27");var subQ6=sQuery(id+"F0.wireOp",EDGE,"E5");var subQ7=makeQuery(id+"F0.imprint","INTERSECT",VERTEX,{"derivedFrom":[subQ6,subQ5]});Q3=makeQuery(id+"F0.imprint","IMPRINT",FACE,{"disambiguationData":[TD([[makeQuery(id+"F0.imprint","IMPRINT",EDGE,{"disambiguationData":[TD([[subQ7,1.0]])],"derivedFrom":subQ6}),-1.0]])]});}
            var Q4;
            {var subQ0=sQuery(id+"F0.wireOp",EDGE,"E98.MirrorCS");var subQ1=sQuery(id+"F0.wireOp",EDGE,"E27");var subQ2=makeQuery(id+"F0.imprint","INTERSECT",VERTEX,{"derivedFrom":[subQ1,subQ0]});Q4=makeQuery(id+"F0.imprint","IMPRINT",FACE,{"disambiguationData":[TD([[makeQuery(id+"F0.imprint","IMPRINT",EDGE,{"disambiguationData":[TD([[subQ2,-1.0]])],"derivedFrom":subQ1}),-1.0]])]});}
            var Q5;
            {var subQ0=sQuery(id+"F0.wireOp",EDGE,"E84.MirrorCS");var subQ1=sQuery(id+"F0.wireOp",EDGE,"E5");var subQ2=makeQuery(id+"F0.imprint","INTERSECT",VERTEX,{"derivedFrom":[subQ1,subQ0]});Q5=makeQuery(id+"F0.imprint","IMPRINT",FACE,{"disambiguationData":[TD([[makeQuery(id+"F0.imprint","IMPRINT",EDGE,{"disambiguationData":[TD([[subQ2,-1.0]])],"derivedFrom":subQ1}),-1.0]])]});}
            extrude(context, id + "F18", {"entities" : qUnion([Q0, Q1, Q2, Q3, Q4, Q5]), "depth" : 25.4 * mm, "offsetDistance" : 25.4 * mm});
        }
        {
            var Q0;
            {var subQ0=sQuery(id+"F0.wireOp",EDGE,"E27");var subQ1=sQuery(id+"F0.wireOp",EDGE,"E5");var subQ2=makeQuery(id+"F0.imprint","INTERSECT",VERTEX,{"derivedFrom":[subQ1,subQ0]});Q0=makeQuery(id+"F0.imprint","IMPRINT",FACE,{"disambiguationData":[TD([[makeQuery(id+"F0.imprint","IMPRINT",EDGE,{"disambiguationData":[TD([[subQ2,-1.0]])],"derivedFrom":subQ1}),-1.0]])]});}
            var Q1;
            {var subQ3=sQuery(id+"F0.wireOp",EDGE,"E71.MirrorCS");var subQ9=sQuery(id+"F0.wireOp",EDGE,"E4.0");var subQ10=makeQuery(id+"F0.imprint","INTERSECT",VERTEX,{"derivedFrom":[subQ9,subQ3]});Q1=makeQuery(id+"F0.imprint","IMPRINT",FACE,{"disambiguationData":[TD([[makeQuery(id+"F0.imprint","IMPRINT",EDGE,{"disambiguationData":[TD([[subQ10,-1.0]])],"derivedFrom":subQ9}),1.0]])]});}
            var Q2;
            {var subQ0=sQuery(id+"F0.wireOp",EDGE,"E22");var subQ1=sQuery(id+"F0.wireOp",EDGE,"E4.0");var subQ2=makeQuery(id+"F0.imprint","INTERSECT",VERTEX,{"derivedFrom":[subQ1,subQ0]});Q2=makeQuery(id+"F0.imprint","IMPRINT",FACE,{"disambiguationData":[TD([[makeQuery(id+"F0.imprint","IMPRINT",EDGE,{"disambiguationData":[TD([[subQ2,1.0]])],"derivedFrom":subQ1}),1.0]])]});}
            var Q3;
            {var subQ0=sQuery(id+"F0.wireOp",EDGE,"E27");var subQ1=sQuery(id+"F0.wireOp",EDGE,"E4.0");var subQ2=makeQuery(id+"F0.imprint","INTERSECT",VERTEX,{"derivedFrom":[subQ1,subQ0]});Q3=makeQuery(id+"F0.imprint","IMPRINT",FACE,{"disambiguationData":[TD([[makeQuery(id+"F0.imprint","IMPRINT",EDGE,{"disambiguationData":[TD([[subQ2,-1.0]])],"derivedFrom":subQ1}),1.0]])]});}
            extrude(context, id + "F19", {"entities" : qUnion([Q0, Q1, Q2, Q3]), "depth" : 25.4 * mm, "offsetDistance" : 25.4 * mm});
        }
        {
            var Q0;
            {var subQ0=sQuery(id+"F0.wireOp",EDGE,"E80.MirrorCS");var subQ1=sQuery(id+"F0.wireOp",EDGE,"E28");var subQ2=makeQuery(id+"F0.imprint","INTERSECT",VERTEX,{"derivedFrom":[subQ1,subQ0]});Q0=makeQuery(id+"F0.imprint","IMPRINT",FACE,{"disambiguationData":[TD([[makeQuery(id+"F0.imprint","IMPRINT",EDGE,{"disambiguationData":[TD([[subQ2,-1.0]])],"derivedFrom":subQ1}),-1.0]])]});}
            var Q1;
            {var subQ1=sQuery(id+"F0.wireOp",EDGE,"E4.0");var subQ5=sQuery(id+"F0.wireOp",EDGE,"E28");var subQ6=makeQuery(id+"F0.imprint","INTERSECT",VERTEX,{"derivedFrom":[subQ1,subQ5]});Q1=makeQuery(id+"F0.imprint","IMPRINT",FACE,{"disambiguationData":[TD([[makeQuery(id+"F0.imprint","IMPRINT",EDGE,{"disambiguationData":[TD([[subQ6,-1.0]])],"derivedFrom":subQ1}),1.0]])]});}
            var Q2;
            {var subQ0=sQuery(id+"F0.wireOp",EDGE,"E60.MirrorCS");var subQ1=sQuery(id+"F0.wireOp",EDGE,"E29");var subQ2=makeQuery(id+"F0.imprint","INTERSECT",VERTEX,{"derivedFrom":[subQ1,subQ0]});Q2=makeQuery(id+"F0.imprint","IMPRINT",FACE,{"disambiguationData":[TD([[makeQuery(id+"F0.imprint","IMPRINT",EDGE,{"disambiguationData":[TD([[subQ2,1.0]])],"derivedFrom":subQ1}),1.0]])]});}
            extrude(context, id + "F20", {"entities" : qUnion([Q0, Q1, Q2]), "depth" : 25.4 * mm, "offsetDistance" : 25.4 * mm});
        }
        {
            var Q0;
            {var subQ5=sQuery(id+"F0.wireOp",EDGE,"E22");var subQ6=sQuery(id+"F0.wireOp",EDGE,"E4.0");var subQ7=makeQuery(id+"F0.imprint","INTERSECT",VERTEX,{"derivedFrom":[subQ6,subQ5]});Q0=makeQuery(id+"F0.imprint","IMPRINT",FACE,{"disambiguationData":[TD([[makeQuery(id+"F0.imprint","IMPRINT",EDGE,{"disambiguationData":[TD([[subQ7,-1.0]])],"derivedFrom":subQ6}),1.0]])]});}
            var Q1;
            {var subQ0=sQuery(id+"F0.wireOp",EDGE,"E76.MirrorCS");var subQ1=sQuery(id+"F0.wireOp",EDGE,"E22");var subQ2=makeQuery(id+"F0.imprint","INTERSECT",VERTEX,{"derivedFrom":[subQ1,subQ0]});Q1=makeQuery(id+"F0.imprint","IMPRINT",FACE,{"disambiguationData":[TD([[makeQuery(id+"F0.imprint","IMPRINT",EDGE,{"disambiguationData":[TD([[subQ2,-1.0]])],"derivedFrom":subQ1}),-1.0]])]});}
            var Q2;
            {var subQ0=sQuery(id+"F0.wireOp",EDGE,"E28");var subQ1=sQuery(id+"F0.wireOp",EDGE,"E4.0");var subQ2=makeQuery(id+"F0.imprint","INTERSECT",VERTEX,{"derivedFrom":[subQ1,subQ0]});Q2=makeQuery(id+"F0.imprint","IMPRINT",FACE,{"disambiguationData":[TD([[makeQuery(id+"F0.imprint","IMPRINT",EDGE,{"disambiguationData":[TD([[subQ2,1.0]])],"derivedFrom":subQ1}),1.0]])]});}
            extrude(context, id + "F21", {"entities" : qUnion([Q0, Q1, Q2]), "depth" : 25.4 * mm, "offsetDistance" : 25.4 * mm});
        }
        {
            var Q0;
            {var subQ4=sQuery(id+"F0.wireOp",EDGE,"E3");var subQ5=sQuery(id+"F0.wireOp",EDGE,"E0.bottom");var subQ6=makeQuery(id+"F0.imprint","INTERSECT",VERTEX,{"derivedFrom":[subQ5,subQ4]});Q0=makeQuery(id+"F0.imprint","IMPRINT",FACE,{"disambiguationData":[TD([[makeQuery(id+"F0.imprint","IMPRINT",EDGE,{"disambiguationData":[TD([[subQ6,-1.0]])],"derivedFrom":subQ5}),-1.0]])]});}
            var Q1;
            {var subQ0=sQuery(id+"F0.wireOp",EDGE,"E29");var subQ1=sQuery(id+"F0.wireOp",EDGE,"E4.0");var subQ2=makeQuery(id+"F0.imprint","INTERSECT",VERTEX,{"derivedFrom":[subQ1,subQ0]});Q1=makeQuery(id+"F0.imprint","IMPRINT",FACE,{"disambiguationData":[TD([[makeQuery(id+"F0.imprint","IMPRINT",EDGE,{"disambiguationData":[TD([[subQ2,-1.0]])],"derivedFrom":subQ1}),1.0]])]});}
            extrude(context, id + "F22", {"entities" : qUnion([Q0, Q1]), "depth" : 25.4 * mm, "offsetDistance" : 25.4 * mm});
        }
        {
            var Q0;
            {var subQ1=sQuery(id+"F0.wireOp",EDGE,"E2");var subQ5=makeQuery(id+"F0.imprint","INTERSECT",VERTEX,{"derivedFrom":[subQ1,sQuery(id+"F0.wireOp",EDGE,"E19")]});Q0=makeQuery(id+"F0.imprint","IMPRINT",FACE,{"disambiguationData":[TD([[makeQuery(id+"F0.imprint","IMPRINT",EDGE,{"disambiguationData":[TD([[subQ5,1.0]])],"derivedFrom":subQ1}),1.0]])]});}
            var Q1;
            {var subQ0=sQuery(id+"F0.wireOp",EDGE,"E87.MirrorCS");Q1=makeQuery(id+"F0.imprint","IMPRINT",FACE,{"disambiguationData":[TD([[makeQuery(id+"F0.imprint","IMPRINT",EDGE,{"derivedFrom":subQ0}),1.0]])]});}
            extrude(context, id + "F23", {"entities" : qUnion([Q0, Q1]), "depth" : 25.4 * mm, "offsetDistance" : 25.4 * mm});
        }
        {
            var Q0;
            {var subQ0=sQuery(id+"F0.wireOp",EDGE,"E84.MirrorCS");var subQ1=sQuery(id+"F0.wireOp",EDGE,"E5");var subQ2=makeQuery(id+"F0.imprint","INTERSECT",VERTEX,{"derivedFrom":[subQ1,subQ0]});Q0=makeQuery(id+"F0.imprint","IMPRINT",FACE,{"disambiguationData":[TD([[makeQuery(id+"F0.imprint","IMPRINT",EDGE,{"disambiguationData":[TD([[subQ2,-1.0]])],"derivedFrom":subQ1}),1.0]])]});}
            var Q1;
            {var subQ5=sQuery(id+"F0.wireOp",EDGE,"E5");var subQ6=makeQuery(id+"F0.imprint","INTERSECT",VERTEX,{"derivedFrom":[subQ5,sQuery(id+"F0.wireOp",EDGE,"E27")]});Q1=makeQuery(id+"F0.imprint","IMPRINT",FACE,{"disambiguationData":[TD([[makeQuery(id+"F0.imprint","IMPRINT",EDGE,{"disambiguationData":[TD([[subQ6,1.0]])],"derivedFrom":subQ5}),1.0]])]});}
            var Q2;
            {var subQ0=sQuery(id+"F0.wireOp",EDGE,"E98.MirrorCS");var subQ1=sQuery(id+"F0.wireOp",EDGE,"E5");var subQ2=makeQuery(id+"F0.imprint","INTERSECT",VERTEX,{"derivedFrom":[subQ1,subQ0]});Q2=makeQuery(id+"F0.imprint","IMPRINT",FACE,{"disambiguationData":[TD([[makeQuery(id+"F0.imprint","IMPRINT",EDGE,{"disambiguationData":[TD([[subQ2,-1.0]])],"derivedFrom":subQ1}),1.0]])]});}
            extrude(context, id + "F24", {"entities" : qUnion([Q0, Q1, Q2]), "depth" : 25.4 * mm, "offsetDistance" : 25.4 * mm});
        }
        {
            var Q0;
            {var subQ0=sQuery(id+"F0.wireOp",EDGE,"E61.MirrorCS");var subQ35=makeQuery(id+"F0.imprint","IMPRINT",VERTEX,{"derivedFrom":subQ0});Q0=makeQuery(id+"F0.imprint","IMPRINT",FACE,{"disambiguationData":[TD([[makeQuery(id+"F0.imprint","IMPRINT",EDGE,{"disambiguationData":[TD([[subQ35,1.0]])],"derivedFrom":subQ0}),-1.0]])]});}
            var Q1;
            {var subQ0=sQuery(id+"F0.wireOp",EDGE,"E61.MirrorCS");var subQ1=sQuery(id+"F0.wireOp",EDGE,"E0.top");var subQ2=makeQuery(id+"F0.imprint","INTERSECT",VERTEX,{"derivedFrom":[subQ1,subQ0]});Q1=makeQuery(id+"F0.imprint","IMPRINT",FACE,{"disambiguationData":[TD([[makeQuery(id+"F0.imprint","IMPRINT",EDGE,{"disambiguationData":[TD([[subQ2,-1.0]])],"derivedFrom":subQ1}),1.0]])]});}
            extrude(context, id + "F25", {"entities" : qUnion([Q0, Q1]), "depth" : 25.4 * mm, "offsetDistance" : 25.4 * mm});
        }
        {
            var Q0;
            {var subQ0=sQuery(id+"F0.wireOp",EDGE,"E61.MirrorCS");var subQ1=sQuery(id+"F0.wireOp",EDGE,"E0.top");var subQ2=makeQuery(id+"F0.imprint","INTERSECT",VERTEX,{"derivedFrom":[subQ1,subQ0]});Q0=makeQuery(id+"F0.imprint","IMPRINT",FACE,{"disambiguationData":[TD([[makeQuery(id+"F0.imprint","IMPRINT",EDGE,{"disambiguationData":[TD([[subQ2,1.0]])],"derivedFrom":subQ1}),1.0]])]});}
            var Q1;
            {var subQ0=sQuery(id+"F0.wireOp",EDGE,"E64.MirrorCS");var subQ1=sQuery(id+"F0.wireOp",EDGE,"E0.top");var subQ2=makeQuery(id+"F0.imprint","INTERSECT",VERTEX,{"derivedFrom":[subQ1,subQ0]});Q1=makeQuery(id+"F0.imprint","IMPRINT",FACE,{"disambiguationData":[TD([[makeQuery(id+"F0.imprint","IMPRINT",EDGE,{"disambiguationData":[TD([[subQ2,1.0]])],"derivedFrom":subQ1}),1.0]])]});}
            var Q2;
            {var subQ0=sQuery(id+"F0.wireOp",EDGE,"E64.MirrorCS");var subQ1=sQuery(id+"F0.wireOp",EDGE,"E61.MirrorCS");var subQ2=makeQuery(id+"F0.imprint","INTERSECT",VERTEX,{"derivedFrom":[subQ1,subQ0]});Q2=makeQuery(id+"F0.imprint","IMPRINT",FACE,{"disambiguationData":[TD([[makeQuery(id+"F0.imprint","IMPRINT",EDGE,{"disambiguationData":[TD([[subQ2,-1.0]])],"derivedFrom":subQ1}),1.0]])]});}
            var Q3;
            {var subQ0=sQuery(id+"F0.wireOp",EDGE,"E64.MirrorCS");var subQ1=sQuery(id+"F0.wireOp",EDGE,"E61.MirrorCS");var subQ2=makeQuery(id+"F0.imprint","INTERSECT",VERTEX,{"derivedFrom":[subQ1,subQ0]});Q3=makeQuery(id+"F0.imprint","IMPRINT",FACE,{"disambiguationData":[TD([[makeQuery(id+"F0.imprint","IMPRINT",EDGE,{"disambiguationData":[TD([[subQ2,1.0]])],"derivedFrom":subQ1}),1.0]])]});}
            extrude(context, id + "F26", {"entities" : qUnion([Q0, Q1, Q2, Q3]), "depth" : 25.4 * mm, "offsetDistance" : 25.4 * mm});
        }
        {
            var Q0;
            {var subQ5=sQuery(id+"F0.wireOp",EDGE,"E78.MirrorCS");Q0=makeQuery(id+"F0.imprint","IMPRINT",FACE,{"disambiguationData":[TD([[makeQuery(id+"F0.imprint","IMPRINT",EDGE,{"derivedFrom":subQ5}),-1.0]])]});}
            var Q1;
            {var subQ0=sQuery(id+"F0.wireOp",EDGE,"E78.MirrorCS");Q1=makeQuery(id+"F0.imprint","IMPRINT",FACE,{"disambiguationData":[TD([[makeQuery(id+"F0.imprint","IMPRINT",EDGE,{"derivedFrom":subQ0}),1.0]])]});}
            extrude(context, id + "F27", {"entities" : qUnion([Q0, Q1]), "depth" : 25.4 * mm, "offsetDistance" : 25.4 * mm});
        }
        {
            var Q0;
            {var subQ0=sQuery(id+"F0.wireOp",EDGE,"E95.MirrorCS");var subQ1=sQuery(id+"F0.wireOp",EDGE,"E0.left");var subQ2=makeQuery(id+"F0.imprint","INTERSECT",VERTEX,{"derivedFrom":[subQ1,subQ0]});Q0=makeQuery(id+"F0.imprint","IMPRINT",FACE,{"disambiguationData":[TD([[makeQuery(id+"F0.imprint","IMPRINT",EDGE,{"disambiguationData":[TD([[subQ2,-1.0]])],"derivedFrom":subQ1}),1.0]])]});}
            var Q1;
            {var subQ0=sQuery(id+"F0.wireOp",EDGE,"E79.MirrorCS");var subQ1=sQuery(id+"F0.wireOp",EDGE,"E0.left");var subQ2=makeQuery(id+"F0.imprint","INTERSECT",VERTEX,{"derivedFrom":[subQ1,subQ0]});Q1=makeQuery(id+"F0.imprint","IMPRINT",FACE,{"disambiguationData":[TD([[makeQuery(id+"F0.imprint","IMPRINT",EDGE,{"disambiguationData":[TD([[subQ2,-1.0]])],"derivedFrom":subQ1}),1.0]])]});}
            extrude(context, id + "F28", {"entities" : qUnion([Q0, Q1]), "depth" : 25.4 * mm, "offsetDistance" : 25.4 * mm});
        }
        {
            var Q0;
            {var subQ0=sQuery(id+"F0.wireOp",EDGE,"E85.MirrorCS");var subQ1=sQuery(id+"F0.wireOp",EDGE,"E0.left");var subQ2=makeQuery(id+"F0.imprint","INTERSECT",VERTEX,{"derivedFrom":[subQ1,subQ0]});Q0=makeQuery(id+"F0.imprint","IMPRINT",FACE,{"disambiguationData":[TD([[makeQuery(id+"F0.imprint","IMPRINT",EDGE,{"disambiguationData":[TD([[subQ2,-1.0]])],"derivedFrom":subQ1}),1.0]])]});}
            var Q1;
            {var subQ0=sQuery(id+"F0.wireOp",EDGE,"E110.MirrorCS");var subQ1=sQuery(id+"F0.wireOp",EDGE,"E0.left");var subQ2=makeQuery(id+"F0.imprint","INTERSECT",VERTEX,{"derivedFrom":[subQ1,subQ0]});Q1=makeQuery(id+"F0.imprint","IMPRINT",FACE,{"disambiguationData":[TD([[makeQuery(id+"F0.imprint","IMPRINT",EDGE,{"disambiguationData":[TD([[subQ2,-1.0]])],"derivedFrom":subQ1}),1.0]])]});}
            extrude(context, id + "F29", {"entities" : qUnion([Q0, Q1]), "depth" : 25.4 * mm, "offsetDistance" : 25.4 * mm});
        }
        {
            var Q0;
            {var subQ0=sQuery(id+"F0.wireOp",EDGE,"E105.MirrorCS");var subQ1=sQuery(id+"F0.wireOp",EDGE,"E0.left");var subQ2=makeQuery(id+"F0.imprint","INTERSECT",VERTEX,{"derivedFrom":[subQ1,subQ0]});Q0=makeQuery(id+"F0.imprint","IMPRINT",FACE,{"disambiguationData":[TD([[makeQuery(id+"F0.imprint","IMPRINT",EDGE,{"disambiguationData":[TD([[subQ2,-1.0]])],"derivedFrom":subQ1}),1.0]])]});}
            var Q1;
            {var subQ1=sQuery(id+"F0.wireOp",EDGE,"E65.MirrorCS");Q1=makeQuery(id+"F0.imprint","IMPRINT",FACE,{"disambiguationData":[TD([[makeQuery(id+"F0.imprint","IMPRINT",EDGE,{"derivedFrom":subQ1}),1.0]])]});}
            extrude(context, id + "F30", {"entities" : qUnion([Q0, Q1]), "depth" : 25.4 * mm, "offsetDistance" : 25.4 * mm});
        }
        {
            var Q0;
            {var subQ0=sQuery(id+"F0.wireOp",EDGE,"E65.MirrorCS");Q0=makeQuery(id+"F0.imprint","IMPRINT",FACE,{"disambiguationData":[TD([[makeQuery(id+"F0.imprint","IMPRINT",EDGE,{"derivedFrom":subQ0}),-1.0]])]});}
            var Q1;
            {var subQ0=sQuery(id+"F0.wireOp",EDGE,"E70.MirrorCS");Q1=makeQuery(id+"F0.imprint","IMPRINT",FACE,{"disambiguationData":[TD([[makeQuery(id+"F0.imprint","IMPRINT",EDGE,{"derivedFrom":subQ0}),-1.0]])]});}
            extrude(context, id + "F31", {"entities" : qUnion([Q0, Q1]), "depth" : 25.4 * mm, "offsetDistance" : 25.4 * mm});
        }
        {
            var Q0;
            {var subQ0=sQuery(id+"F0.wireOp",EDGE,"E1");var subQ1=makeQuery(id+"F0.imprint","INTERSECT",VERTEX,{"derivedFrom":[subQ0,sQuery(id+"F0.wireOp",EDGE,"E23")]});Q0=makeQuery(id+"F0.imprint","IMPRINT",FACE,{"disambiguationData":[TD([[makeQuery(id+"F0.imprint","IMPRINT",EDGE,{"disambiguationData":[TD([[subQ1,1.0]])],"derivedFrom":subQ0}),1.0]])]});}
            extrude(context, id + "F32", {"entities" : qUnion([Q0]), "depth" : 25.4 * mm, "offsetDistance" : 25.4 * mm});
        }
        {
            var Q0;
            {var subQ0=sQuery(id+"F0.wireOp",EDGE,"E0.left");var subQ1=sQuery(id+"F0.wireOp",EDGE,"E0.top");var subQ2=makeQuery(id+"F0.imprint","INTERSECT",VERTEX,{"derivedFrom":[subQ1,subQ0]});Q0=makeQuery(id+"F0.imprint","IMPRINT",FACE,{"disambiguationData":[TD([[makeQuery(id+"F0.imprint","IMPRINT",EDGE,{"disambiguationData":[TD([[subQ2,-1.0]])],"derivedFrom":subQ1}),1.0]])]});}
            extrude(context, id + "F33", {"entities" : qUnion([Q0]), "depth" : 25.4 * mm, "offsetDistance" : 25.4 * mm});
        }
        {
            var Q0;
            {var subQ0=sQuery(id+"F0.wireOp",EDGE,"E0.right");var subQ1=sQuery(id+"F0.wireOp",EDGE,"E0.bottom");var subQ2=makeQuery(id+"F0.imprint","INTERSECT",VERTEX,{"derivedFrom":[subQ1,subQ0]});Q0=makeQuery(id+"F0.imprint","IMPRINT",FACE,{"disambiguationData":[TD([[makeQuery(id+"F0.imprint","IMPRINT",EDGE,{"disambiguationData":[TD([[subQ2,1.0]])],"derivedFrom":subQ1}),-1.0]])]});}
            extrude(context, id + "F34", {"entities" : qUnion([Q0]), "depth" : 25.4 * mm, "offsetDistance" : 25.4 * mm});
        }
        {
            var Q0;
            {var subQ3=sQuery(id+"F0.wireOp",EDGE,"E0.left");var subQ5=sQuery(id+"F0.wireOp",EDGE,"E0.bottom");var subQ6=makeQuery(id+"F0.imprint","INTERSECT",VERTEX,{"derivedFrom":[subQ5,subQ3]});Q0=makeQuery(id+"F0.imprint","IMPRINT",FACE,{"disambiguationData":[TD([[makeQuery(id+"F0.imprint","IMPRINT",EDGE,{"disambiguationData":[TD([[subQ6,-1.0]])],"derivedFrom":subQ5}),-1.0]])]});}
            extrude(context, id + "F35", {"entities" : qUnion([Q0]), "depth" : 25.4 * mm, "offsetDistance" : 25.4 * mm});
        }
        {
            var Q0;
            {var subQ5=sQuery(id+"F0.wireOp",EDGE,"E120");Q0=makeQuery(id+"F0.imprint","IMPRINT",FACE,{"disambiguationData":[TD([[makeQuery(id+"F0.imprint","IMPRINT",EDGE,{"derivedFrom":subQ5}),-1.0]])]});}
            var Q1;
            {var subQ0=sQuery(id+"F0.wireOp",EDGE,"E92.MirrorCS");var subQ1=sQuery(id+"F0.wireOp",EDGE,"E0.top");var subQ2=makeQuery(id+"F0.imprint","INTERSECT",VERTEX,{"derivedFrom":[subQ1,subQ0]});Q1=makeQuery(id+"F0.imprint","IMPRINT",FACE,{"disambiguationData":[TD([[makeQuery(id+"F0.imprint","IMPRINT",EDGE,{"disambiguationData":[TD([[subQ2,-1.0]])],"derivedFrom":subQ1}),-1.0]])]});}
            var Q2;
            {var subQ0=sQuery(id+"F0.wireOp",EDGE,"E77.MirrorCS");var subQ1=sQuery(id+"F0.wireOp",EDGE,"E0.top");var subQ2=makeQuery(id+"F0.imprint","INTERSECT",VERTEX,{"derivedFrom":[subQ1,subQ0]});Q2=makeQuery(id+"F0.imprint","IMPRINT",FACE,{"disambiguationData":[TD([[makeQuery(id+"F0.imprint","IMPRINT",EDGE,{"disambiguationData":[TD([[subQ2,-1.0]])],"derivedFrom":subQ1}),-1.0]])]});}
            var Q3;
            {var subQ3=sQuery(id+"F0.wireOp",EDGE,"E0.top");var subQ8=makeQuery(id+"F0.imprint","INTERSECT",VERTEX,{"derivedFrom":[subQ3,sQuery(id+"F0.wireOp",EDGE,"E61.MirrorCS")]});Q3=makeQuery(id+"F0.imprint","IMPRINT",FACE,{"disambiguationData":[TD([[makeQuery(id+"F0.imprint","IMPRINT",EDGE,{"disambiguationData":[TD([[subQ8,1.0]])],"derivedFrom":subQ3}),-1.0]])]});}
            var Q4;
            {var subQ0=sQuery(id+"F0.wireOp",EDGE,"E74.MirrorCS");var subQ3=sQuery(id+"F0.wireOp",EDGE,"E0.top");var subQ4=makeQuery(id+"F0.imprint","INTERSECT",VERTEX,{"derivedFrom":[subQ3,subQ0]});Q4=makeQuery(id+"F0.imprint","IMPRINT",FACE,{"disambiguationData":[TD([[makeQuery(id+"F0.imprint","IMPRINT",EDGE,{"disambiguationData":[TD([[subQ4,-1.0]])],"derivedFrom":subQ3}),-1.0]])]});}
            var Q5;
            {var subQ0=sQuery(id+"F0.wireOp",EDGE,"E69.MirrorCS");var subQ1=sQuery(id+"F0.wireOp",EDGE,"E0.top");var subQ2=makeQuery(id+"F0.imprint","INTERSECT",VERTEX,{"derivedFrom":[subQ1,subQ0]});Q5=makeQuery(id+"F0.imprint","IMPRINT",FACE,{"disambiguationData":[TD([[makeQuery(id+"F0.imprint","IMPRINT",EDGE,{"disambiguationData":[TD([[subQ2,-1.0]])],"derivedFrom":subQ1}),-1.0]])]});}
            var Q6;
            {var subQ0=sQuery(id+"F0.wireOp",EDGE,"E121");Q6=makeQuery(id+"F0.imprint","IMPRINT",FACE,{"disambiguationData":[TD([[makeQuery(id+"F0.imprint","IMPRINT",EDGE,{"derivedFrom":subQ0}),1.0]])]});}
            extrude(context, id + "F36", {"entities" : qUnion([Q0, Q1, Q2, Q3, Q4, Q5, Q6]), "depth" : 25.4 * mm, "offsetDistance" : 25.4 * mm});
        }
        {
            var Q0;
            {var subQ0=sQuery(id+"F0.wireOp",EDGE,"E121");Q0=makeQuery(id+"F0.imprint","IMPRINT",FACE,{"disambiguationData":[TD([[makeQuery(id+"F0.imprint","IMPRINT",EDGE,{"derivedFrom":subQ0}),-1.0]])]});}
            var Q1;
            {var subQ0=sQuery(id+"F0.wireOp",EDGE,"E107.MirrorCS");var subQ1=sQuery(id+"F0.wireOp",EDGE,"E0.left");var subQ2=makeQuery(id+"F0.imprint","INTERSECT",VERTEX,{"derivedFrom":[subQ1,subQ0]});Q1=makeQuery(id+"F0.imprint","IMPRINT",FACE,{"disambiguationData":[TD([[makeQuery(id+"F0.imprint","IMPRINT",EDGE,{"disambiguationData":[TD([[subQ2,-1.0]])],"derivedFrom":subQ1}),-1.0]])]});}
            var Q2;
            {var subQ3=sQuery(id+"F0.wireOp",EDGE,"E0.left");var subQ5=sQuery(id+"F0.wireOp",EDGE,"E95.MirrorCS");var subQ6=makeQuery(id+"F0.imprint","INTERSECT",VERTEX,{"derivedFrom":[subQ3,subQ5]});Q2=makeQuery(id+"F0.imprint","IMPRINT",FACE,{"disambiguationData":[TD([[makeQuery(id+"F0.imprint","IMPRINT",EDGE,{"disambiguationData":[TD([[subQ6,-1.0]])],"derivedFrom":subQ3}),-1.0]])]});}
            var Q3;
            {var subQ0=sQuery(id+"F0.wireOp",EDGE,"E79.MirrorCS");var subQ1=sQuery(id+"F0.wireOp",EDGE,"E0.left");var subQ2=makeQuery(id+"F0.imprint","INTERSECT",VERTEX,{"derivedFrom":[subQ1,subQ0]});Q3=makeQuery(id+"F0.imprint","IMPRINT",FACE,{"disambiguationData":[TD([[makeQuery(id+"F0.imprint","IMPRINT",EDGE,{"disambiguationData":[TD([[subQ2,-1.0]])],"derivedFrom":subQ1}),-1.0]])]});}
            var Q4;
            {var subQ0=sQuery(id+"F0.wireOp",EDGE,"E110.MirrorCS");var subQ1=sQuery(id+"F0.wireOp",EDGE,"E0.left");var subQ2=makeQuery(id+"F0.imprint","INTERSECT",VERTEX,{"derivedFrom":[subQ1,subQ0]});Q4=makeQuery(id+"F0.imprint","IMPRINT",FACE,{"disambiguationData":[TD([[makeQuery(id+"F0.imprint","IMPRINT",EDGE,{"disambiguationData":[TD([[subQ2,-1.0]])],"derivedFrom":subQ1}),-1.0]])]});}
            var Q5;
            {var subQ1=sQuery(id+"F0.wireOp",EDGE,"E85.MirrorCS");var subQ6=sQuery(id+"F0.wireOp",EDGE,"E0.left");var subQ9=makeQuery(id+"F0.imprint","INTERSECT",VERTEX,{"derivedFrom":[subQ6,subQ1]});Q5=makeQuery(id+"F0.imprint","IMPRINT",FACE,{"disambiguationData":[TD([[makeQuery(id+"F0.imprint","IMPRINT",EDGE,{"disambiguationData":[TD([[subQ9,-1.0]])],"derivedFrom":subQ6}),-1.0]])]});}
            var Q6;
            {var subQ0=sQuery(id+"F0.wireOp",EDGE,"E105.MirrorCS");var subQ1=sQuery(id+"F0.wireOp",EDGE,"E0.left");var subQ2=makeQuery(id+"F0.imprint","INTERSECT",VERTEX,{"derivedFrom":[subQ1,subQ0]});Q6=makeQuery(id+"F0.imprint","IMPRINT",FACE,{"disambiguationData":[TD([[makeQuery(id+"F0.imprint","IMPRINT",EDGE,{"disambiguationData":[TD([[subQ2,-1.0]])],"derivedFrom":subQ1}),-1.0]])]});}
            var Q7;
            {var subQ8=sQuery(id+"F0.wireOp",EDGE,"E122");Q7=makeQuery(id+"F0.imprint","IMPRINT",FACE,{"disambiguationData":[TD([[makeQuery(id+"F0.imprint","IMPRINT",EDGE,{"derivedFrom":subQ8}),1.0]])]});}
            var Q8;
            {var subQ0=sQuery(id+"F0.wireOp",EDGE,"E83.MirrorCS");var subQ1=sQuery(id+"F0.wireOp",EDGE,"E0.left");var subQ2=makeQuery(id+"F0.imprint","INTERSECT",VERTEX,{"derivedFrom":[subQ1,subQ0]});Q8=makeQuery(id+"F0.imprint","IMPRINT",FACE,{"disambiguationData":[TD([[makeQuery(id+"F0.imprint","IMPRINT",EDGE,{"disambiguationData":[TD([[subQ2,-1.0]])],"derivedFrom":subQ1}),-1.0]])]});}
            extrude(context, id + "F37", {"entities" : qUnion([Q0, Q1, Q2, Q3, Q4, Q5, Q6, Q7, Q8]), "depth" : 25.4 * mm, "offsetDistance" : 25.4 * mm});
        }
        {
            var Q0;
            {var subQ5=sQuery(id+"F0.wireOp",EDGE,"E122");Q0=makeQuery(id+"F0.imprint","IMPRINT",FACE,{"disambiguationData":[TD([[makeQuery(id+"F0.imprint","IMPRINT",EDGE,{"derivedFrom":subQ5}),-1.0]])]});}
            var Q1;
            {var subQ1=sQuery(id+"F0.wireOp",EDGE,"E48.MirrorCS");var subQ3=sQuery(id+"F0.wireOp",EDGE,"E0.bottom");var subQ4=makeQuery(id+"F0.imprint","INTERSECT",VERTEX,{"derivedFrom":[subQ3,subQ1]});Q1=makeQuery(id+"F0.imprint","IMPRINT",FACE,{"disambiguationData":[TD([[makeQuery(id+"F0.imprint","IMPRINT",EDGE,{"disambiguationData":[TD([[subQ4,-1.0]])],"derivedFrom":subQ3}),1.0]])]});}
            var Q2;
            {var subQ0=sQuery(id+"F0.wireOp",EDGE,"E35.MirrorCS");var subQ1=sQuery(id+"F0.wireOp",EDGE,"E0.bottom");var subQ2=makeQuery(id+"F0.imprint","INTERSECT",VERTEX,{"derivedFrom":[subQ1,subQ0]});Q2=makeQuery(id+"F0.imprint","IMPRINT",FACE,{"disambiguationData":[TD([[makeQuery(id+"F0.imprint","IMPRINT",EDGE,{"disambiguationData":[TD([[subQ2,-1.0]])],"derivedFrom":subQ1}),1.0]])]});}
            var Q3;
            {var subQ8=sQuery(id+"F0.wireOp",EDGE,"E123");Q3=makeQuery(id+"F0.imprint","IMPRINT",FACE,{"disambiguationData":[TD([[makeQuery(id+"F0.imprint","IMPRINT",EDGE,{"derivedFrom":subQ8}),1.0]])]});}
            var Q4;
            {var subQ0=sQuery(id+"F0.wireOp",EDGE,"E51.MirrorCS");var subQ1=sQuery(id+"F0.wireOp",EDGE,"E0.bottom");var subQ2=makeQuery(id+"F0.imprint","INTERSECT",VERTEX,{"derivedFrom":[subQ1,subQ0]});Q4=makeQuery(id+"F0.imprint","IMPRINT",FACE,{"disambiguationData":[TD([[makeQuery(id+"F0.imprint","IMPRINT",EDGE,{"disambiguationData":[TD([[subQ2,-1.0]])],"derivedFrom":subQ1}),1.0]])]});}
            extrude(context, id + "F38", {"entities" : qUnion([Q0, Q1, Q2, Q3, Q4]), "depth" : 25.4 * mm, "offsetDistance" : 25.4 * mm});
        }
        {
            var Q0;
            {var subQ0=sQuery(id+"F0.wireOp",EDGE,"E120");Q0=makeQuery(id+"F0.imprint","IMPRINT",FACE,{"disambiguationData":[TD([[makeQuery(id+"F0.imprint","IMPRINT",EDGE,{"derivedFrom":subQ0}),1.0]])]});}
            var Q1;
            {var subQ0=sQuery(id+"F0.wireOp",EDGE,"E49.MirrorCS");var subQ1=sQuery(id+"F0.wireOp",EDGE,"E0.right");var subQ2=makeQuery(id+"F0.imprint","INTERSECT",VERTEX,{"derivedFrom":[subQ1,subQ0]});Q1=makeQuery(id+"F0.imprint","IMPRINT",FACE,{"disambiguationData":[TD([[makeQuery(id+"F0.imprint","IMPRINT",EDGE,{"disambiguationData":[TD([[subQ2,-1.0]])],"derivedFrom":subQ1}),1.0]])]});}
            var Q2;
            {var subQ0=sQuery(id+"F0.wireOp",EDGE,"E34.MirrorCS");var subQ1=sQuery(id+"F0.wireOp",EDGE,"E0.right");var subQ2=makeQuery(id+"F0.imprint","INTERSECT",VERTEX,{"derivedFrom":[subQ1,subQ0]});Q2=makeQuery(id+"F0.imprint","IMPRINT",FACE,{"disambiguationData":[TD([[makeQuery(id+"F0.imprint","IMPRINT",EDGE,{"disambiguationData":[TD([[subQ2,-1.0]])],"derivedFrom":subQ1}),1.0]])]});}
            var Q3;
            {var subQ0=sQuery(id+"F0.wireOp",EDGE,"E50.MirrorCS");var subQ1=sQuery(id+"F0.wireOp",EDGE,"E0.right");var subQ2=makeQuery(id+"F0.imprint","INTERSECT",VERTEX,{"derivedFrom":[subQ1,subQ0]});Q3=makeQuery(id+"F0.imprint","IMPRINT",FACE,{"disambiguationData":[TD([[makeQuery(id+"F0.imprint","IMPRINT",EDGE,{"disambiguationData":[TD([[subQ2,-1.0]])],"derivedFrom":subQ1}),1.0]])]});}
            var Q4;
            {var subQ0=sQuery(id+"F0.wireOp",EDGE,"E47.MirrorCS");var subQ1=sQuery(id+"F0.wireOp",EDGE,"E0.right");var subQ2=makeQuery(id+"F0.imprint","INTERSECT",VERTEX,{"derivedFrom":[subQ1,subQ0]});Q4=makeQuery(id+"F0.imprint","IMPRINT",FACE,{"disambiguationData":[TD([[makeQuery(id+"F0.imprint","IMPRINT",EDGE,{"disambiguationData":[TD([[subQ2,-1.0]])],"derivedFrom":subQ1}),1.0]])]});}
            var Q5;
            {var subQ1=sQuery(id+"F0.wireOp",EDGE,"E42.MirrorCS");var subQ5=sQuery(id+"F0.wireOp",EDGE,"E0.right");var subQ6=makeQuery(id+"F0.imprint","INTERSECT",VERTEX,{"derivedFrom":[subQ5,subQ1]});Q5=makeQuery(id+"F0.imprint","IMPRINT",FACE,{"disambiguationData":[TD([[makeQuery(id+"F0.imprint","IMPRINT",EDGE,{"disambiguationData":[TD([[subQ6,-1.0]])],"derivedFrom":subQ5}),1.0]])]});}
            var Q6;
            {var subQ0=sQuery(id+"F0.wireOp",EDGE,"E32.MirrorCS");var subQ1=sQuery(id+"F0.wireOp",EDGE,"E0.right");var subQ2=makeQuery(id+"F0.imprint","INTERSECT",VERTEX,{"derivedFrom":[subQ1,subQ0]});Q6=makeQuery(id+"F0.imprint","IMPRINT",FACE,{"disambiguationData":[TD([[makeQuery(id+"F0.imprint","IMPRINT",EDGE,{"disambiguationData":[TD([[subQ2,-1.0]])],"derivedFrom":subQ1}),1.0]])]});}
            var Q7;
            {var subQ8=sQuery(id+"F0.wireOp",EDGE,"E123");Q7=makeQuery(id+"F0.imprint","IMPRINT",FACE,{"disambiguationData":[TD([[makeQuery(id+"F0.imprint","IMPRINT",EDGE,{"derivedFrom":subQ8}),-1.0]])]});}
            var Q8;
            {var subQ0=sQuery(id+"F0.wireOp",EDGE,"E39.MirrorCS");var subQ1=sQuery(id+"F0.wireOp",EDGE,"E0.right");var subQ2=makeQuery(id+"F0.imprint","INTERSECT",VERTEX,{"derivedFrom":[subQ1,subQ0]});Q8=makeQuery(id+"F0.imprint","IMPRINT",FACE,{"disambiguationData":[TD([[makeQuery(id+"F0.imprint","IMPRINT",EDGE,{"disambiguationData":[TD([[subQ2,-1.0]])],"derivedFrom":subQ1}),1.0]])]});}
            extrude(context, id + "F39", {"entities" : qUnion([Q0, Q1, Q2, Q3, Q4, Q5, Q6, Q7, Q8]), "depth" : 25.4 * mm, "offsetDistance" : 25.4 * mm});
        }
        {
            var Q0;
            {var subQ0=sQuery(id+"F0.wireOp",EDGE,"E66.MirrorCS");Q0=makeQuery(id+"F0.imprint","IMPRINT",FACE,{"disambiguationData":[TD([[makeQuery(id+"F0.imprint","IMPRINT",EDGE,{"derivedFrom":subQ0}),-1.0]])]});}
            var Q1;
            {var subQ0=sQuery(id+"F0.wireOp",EDGE,"E66.MirrorCS");Q1=makeQuery(id+"F0.imprint","IMPRINT",FACE,{"disambiguationData":[TD([[makeQuery(id+"F0.imprint","IMPRINT",EDGE,{"derivedFrom":subQ0}),1.0]])]});}
            extrude(context, id + "F40", {"entities" : qUnion([Q0, Q1]), "depth" : 25.4 * mm, "offsetDistance" : 25.4 * mm});
        }
        {
            var Q0;
            {var subQ0=sQuery(id+"F0.wireOp",EDGE,"E77.MirrorCS");var subQ1=sQuery(id+"F0.wireOp",EDGE,"E0.top");var subQ2=makeQuery(id+"F0.imprint","INTERSECT",VERTEX,{"derivedFrom":[subQ1,subQ0]});Q0=makeQuery(id+"F0.imprint","IMPRINT",FACE,{"disambiguationData":[TD([[makeQuery(id+"F0.imprint","IMPRINT",EDGE,{"disambiguationData":[TD([[subQ2,-1.0]])],"derivedFrom":subQ1}),1.0]])]});}
            var Q1;
            {var subQ0=sQuery(id+"F0.wireOp",EDGE,"E60.MirrorCS");var subQ1=sQuery(id+"F0.wireOp",EDGE,"E0.top");var subQ2=makeQuery(id+"F0.imprint","INTERSECT",VERTEX,{"derivedFrom":[subQ1,subQ0]});Q1=makeQuery(id+"F0.imprint","IMPRINT",FACE,{"disambiguationData":[TD([[makeQuery(id+"F0.imprint","IMPRINT",EDGE,{"disambiguationData":[TD([[subQ2,-1.0]])],"derivedFrom":subQ1}),1.0]])]});}
            extrude(context, id + "F41", {"entities" : qUnion([Q0, Q1]), "depth" : 25.4 * mm, "offsetDistance" : 25.4 * mm});
        }
    });
